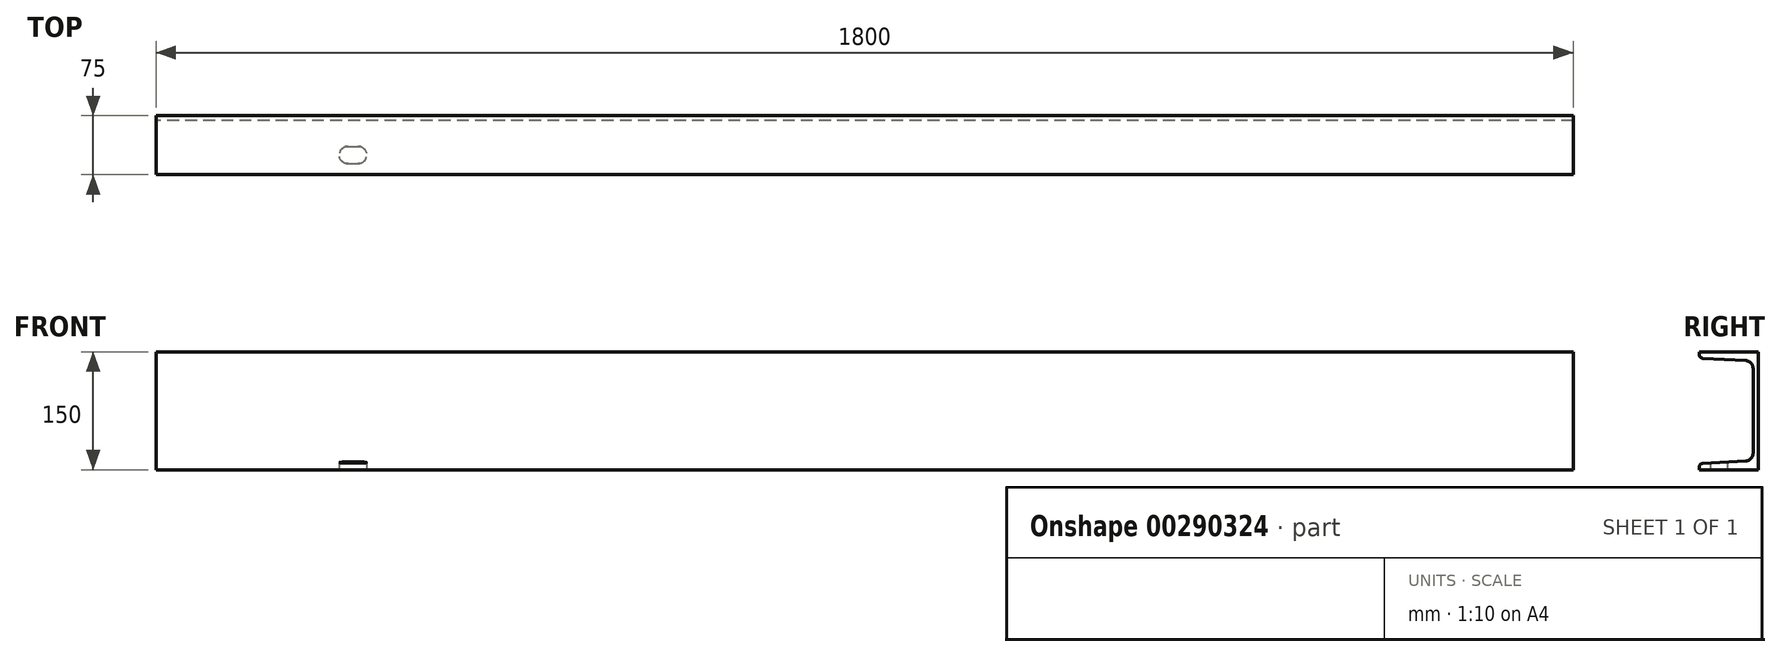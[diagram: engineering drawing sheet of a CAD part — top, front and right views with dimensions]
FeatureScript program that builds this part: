
annotation { "Feature Type Name" : "Feature", "Feature Type Description" : "" }
export const myFeature = defineFeature(function(context is Context, id is Id, definition is map)
    precondition{}
    {
        {
            var Q0;
            Q0=qCreatedBy(makeId("Right.planeOp"),FACE);
            var sketch = newSketch(context, id + "F0", { "sketchPlane" : qUnion([Q0])});
            skLineSegment(sketch, "E0.MirrorCS", {"start": v(110.42, 0) * mm, "end": v(110.42, -3.29) * mm});
            skArc(sketch, "E1.MirrorCS", {"start": v(169.45, -138.87) * mm, "mid": v(176.18, -135.77) * mm, "end": v(178.92, -128.89) * mm});
            skArc(sketch, "E2.MirrorCS", {"start": v(115.16, -141.72) * mm, "mid": v(111.8, -143.27) * mm, "end": v(110.42, -146.71) * mm});
            skArc(sketch, "E3.MirrorCS", {"start": v(169.45, -11.13) * mm, "mid": v(176.18, -14.23) * mm, "end": v(178.92, -21.11) * mm});
            skArc(sketch, "E4.MirrorCS", {"start": v(115.16, -8.28) * mm, "mid": v(111.8, -6.73) * mm, "end": v(110.42, -3.29) * mm});
            skLineSegment(sketch, "E5.MirrorCS", {"start": v(110.42, -150) * mm, "end": v(110.42, -146.71) * mm});
            skPoint(sketch, "E6.MirrorP", {"position": v(185.42, -75) * mm});
            skLineSegment(sketch, "E7.MirrorCS", {"start": v(185.42, -150) * mm, "end": v(185.42, 0) * mm});
            skPoint(sketch, "E8.MirrorP", {"position": v(147.92, -10) * mm});
            skLineSegment(sketch, "E9.MirrorCS", {"start": v(169.45, -138.87) * mm, "end": v(115.16, -141.72) * mm});
            skPoint(sketch, "E10.MirrorP", {"position": v(110.42, -8.03) * mm});
            skLineSegment(sketch, "E11.MirrorCS", {"start": v(110.42, -150) * mm, "end": v(185.42, -150) * mm});
            skPoint(sketch, "E12.MirrorP", {"position": v(110.42, -141.97) * mm});
            skLineSegment(sketch, "E13.MirrorCS", {"start": v(185.42, 0) * mm, "end": v(110.42, 0) * mm});
            skLineSegment(sketch, "E14.MirrorCS", {"start": v(169.45, -11.13) * mm, "end": v(115.16, -8.28) * mm});
            skLineSegment(sketch, "E15.MirrorCS", {"start": v(178.92, -21.11) * mm, "end": v(178.92, -128.89) * mm});
            skPoint(sketch, "E16.MirrorP", {"position": v(147.92, -140) * mm});
            skSolve(sketch);
        }
        {
            var Q0;
            Q0 = qSketchRegion(id + "F0", true);
            extrude(context, id + "F1", {"entities" : qUnion([Q0]), "depth" : 1800 * mm});
        }
        {
            var Q0;
            Q0=makeQuery(id+"F1.opExtrude","SWEPT_FACE",FACE,{"disambiguationData":[OSD([sQuery(id+"F0.wireOp",EDGE,"E11.MirrorCS")])]});
            var sketch = newSketch(context, id + "F2", { "sketchPlane" : qUnion([Q0])});
            skLineSegment(sketch, "E17", {"start": v(243.5, -135.42) * mm, "end": v(256.5, -135.42) * mm});
            skArc(sketch, "E18.0.startCap", {"start": v(243.5, -146.42) * mm, "mid": v(232.5, -135.42) * mm, "end": v(243.5, -124.42) * mm});
            skArc(sketch, "E18.0.endCap", {"start": v(256.5, -124.42) * mm, "mid": v(267.5, -135.42) * mm, "end": v(256.5, -146.42) * mm});
            skLineSegment(sketch, "E18.0.left", {"start": v(243.5, -124.42) * mm, "end": v(256.5, -124.42) * mm});
            skLineSegment(sketch, "E18.0.right", {"start": v(243.5, -146.42) * mm, "end": v(256.5, -146.42) * mm});
            skSolve(sketch);
        }
        {
            var Q0;
            Q0 = qSketchRegion(id + "F2", true);
            extrude(context, id + "F3", {"entities" : qUnion([Q0]), "operationType" : NewBodyOperationType.REMOVE, "endBound" : BoundingType.UP_TO_NEXT, "oppositeDirection" : true, "depth" : 25 * mm});
        }
        {
            var Q0;
            Q0=qCreatedBy(makeId("Right.planeOp"),FACE);
            cPlane(context, id + "F4", {"entities" : qUnion([Q0]), "cplaneType" : CPlaneType.OFFSET, "offset" : 900 * mm, "width" : 150 * mm, "height" : 150 * mm});
        }
    });
